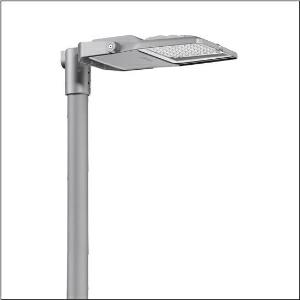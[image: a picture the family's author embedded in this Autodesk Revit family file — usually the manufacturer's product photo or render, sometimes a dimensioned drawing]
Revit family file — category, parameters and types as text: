
# Revit family: floodlight_fl_21_iq_mini___pl52_5xa7772b4d3a_2373
name_source: partatom
category: Lighting Fixtures
units: mm (PartAtom-declared; Revit-internal decimal feet)

## family parameters
Cut with Voids When Loaded = No
Host = Face
Light Source = No
Part Type = Normal
Room Calculation Point = No
Round Connector Dimension = Use Diameter
Shared = No

## types (1)
- --- (1 x LED, 6490 lm, 45.5 W, 4000K)
    Apparent Load = 46 VA
    CIE Flux Codes = 26 60 98 100 100
    Color Rendering = 70
    Color Temperature = 4000K
    Default Elevation = 1800 mm
    Description = Floodlight FL 21 iQ mini, floodlight, primary light control with lens, of PMMA, primary optical cover: protective disc, of toughened safety glass, transparent, light distribution: PL52, light emission: direct distribution, installation type: surface-mounted, LED, High Power LED, rated luminous flux: 6.490lm, luminous efficacy: 143lm/W, light colour: 740, colour temperature: 4000K, control: Auto-Match, Temp-Guard, Night-Set, Smart-Wire, Desk-Remote (wireless, voltage-free reading and setting of iQ features in the workshop via application-optimized NFC function/RFID function), optimised constant luminous flux control (CLO 2.0), Light-Fading, Lumen-Switch, with terminal, 6-pole, mains connection: 220..240V, AC, 50/60Hz, start of lifetime: 46W, end of service life: 48W, reduction: 22W, luminaire housing, of diecast aluminium, powder-coated, Siteco® metallic grey (DB 702S), corrosivity category C5 mid according to DIN EN ISO 12944, sealing non-destructively replaceable, please order mast flange separately, mast bracket, of steel, galvanised, powder-coated, protection rating (complete): IP66, insulation class (complete): insulation class II (safety insulation), certification: CE, ENEC, VDE, protection symbol: D, impact resistance: IK08, permissible operating ambient temperature: -40..+40°C, permissible operating ambient temperature for outdoor applications: -40..+50°C, standard: DIN EN 12944, LABS conformity tested according to VDMA 24364:2018-05, packaging unit: 1 piece

Light Distribution: PL52
    Height = 70 mm
    Lamp = 1 x LED
    Lamp Light Flux = 6490 lm
    Lamp Power = 45.5 W
    Lamp count = 1
    Length = 485 mm
    Luminous efficacy = 143 lm/W
    Manufacturer = Siteco
    ModVariant = No
    Model = 5XA7772B4D3A
    Number of Poles = 1
    OnlyDefault = Yes
    Power Factor = 1
    Product Name = Floodlight FL 21 iQ mini | PL52
    Product group = floodlight | pylon annexe
    ProductGroupID = 6200
    Protection Class = Protection class II
    Protection Degree = IP 66
    RLX_Detail_Level = 1
    RLX_Emergency_Light_Flux = 0 lm
    RLX_Emergency_Type = 0
    RLX_Emergency_Type_DB = No
    RlxData = <blob elided: 101277 chars, md5=b7abb8bc>
    Socket = socket
    Standby Power = 0 W
    System Light Flux = 6490 lm
    System Power = 46 W
    Type Comments = factory setting: luminous flux: 100 % | dim-lin: 254 | 463 mA
    Type Image = l_1007125.jpg
    URL = http://relux.com
    VarID = @adj_096999
    Voltage = 0 V
    Weight = 0.00 kg
    Width = 337 mm

## geometry (parser evidence)
native form markers: Blend x4, Sweep x14
no freeform markers — native parametric forms only
